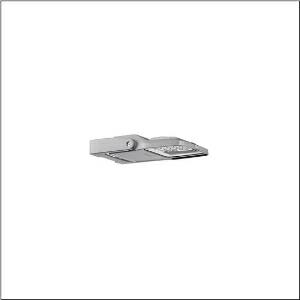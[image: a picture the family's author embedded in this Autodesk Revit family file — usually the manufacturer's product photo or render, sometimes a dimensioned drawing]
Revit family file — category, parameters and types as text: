
# Revit family: floodlight_fl_21_iq_micro___pl33t_5xa7762a2f2a_46b5
name_source: partatom
category: Lighting Fixtures
units: mm (PartAtom-declared; Revit-internal decimal feet)

## family parameters
Cut with Voids When Loaded = No
Host = Face
Light Source = No
Part Type = Normal
Room Calculation Point = No
Round Connector Dimension = Use Diameter
Shared = No

## types (1)
- --- (1 x LED, 2930 lm, 23.1 W, 3000K)
    Apparent Load = 23 VA
    CIE Flux Codes = 26 75 99 100 100
    Color Rendering = 70
    Color Temperature = 3000K
    Default Elevation = 1800 mm
    Description = Floodlight FL 21 iQ micro, floodlight, primary light control with lens, of PMMA, primary optical cover: protective disc, of toughened safety glass, transparent, light distribution: PL33T, light emission: direct distribution, installation type: surface-mounted, LED, High Power LED, rated luminous flux: 2.930lm, luminous efficacy: 127lm/W, light colour: 730, colour temperature: 3000K, control gear: iQ Street-Remote/DALI, control: Auto-Match, Temp-Guard, Night-Set, Smart-Wire, Desk-Remote (wireless, voltage-free reading and setting of iQ features in the workshop via application-optimized NFC function/RFID function), optimised constant luminous flux control (CLO 2.0), Street-Remote, with terminal, 6-pole, mains connection: 220..240V, AC, 50/60Hz, start of lifetime: 23W, end of service life: 24W, reduction: 11W, luminaire housing, of diecast aluminium, powder-coated, Siteco® metallic grey (DB 702S), corrosivity category C5 mid according to DIN EN ISO 12944, suitable for swimming pools, chlorine-resistant, sealing non-destructively replaceable, design bracket, of diecast aluminium, powder-coated, Siteco® metallic grey (DB 702S), protection rating (complete): IP66, insulation class (complete): insulation class II (safety insulation), certification: CE, ENEC, VDE, protection symbol: D, impact resistance: IK07, permissible operating ambient temperature: -40..+40°C, permissible operating ambient temperature for outdoor applications: -40..+50°C, standard: DIN EN 12944, LABS conformity tested according to VDMA 24364:2018-05, packaging unit: 1 piece

Light Distribution: PL33T
    Height = 65 mm
    Lamp = 1 x LED
    Lamp Light Flux = 2930 lm
    Lamp Power = 23.1 W
    Lamp count = 1
    Length = 312 mm
    Luminous efficacy = 127 lm/W
    Manufacturer = Siteco
    ModVariant = No
    Model = 5XA7762A2F2A
    Mounting Place = Wall
    Mounting Type = Surface mounted
    Number of Poles = 1
    OnlyDefault = Yes
    Power Factor = 1
    Product Name = Floodlight FL 21 iQ micro | PL33T
    Product group = floodlight | wall mounted
    ProductGroupID = 2001
    Protection Class = Protection class II
    Protection Degree = IP 66
    RLX_Detail_Level = 1
    RLX_Emergency_Light_Flux = 0 lm
    RLX_Emergency_Type = 0
    RLX_Emergency_Type_DB = No
    RlxData = <blob elided: 97377 chars, md5=efec1c89>
    Socket = socket
    Standby Power = 0 W
    System Light Flux = 2930 lm
    System Power = 23 W
    Type Comments = factory setting: luminous flux: 100 % | dim-lin: 254 | 455 mA
    Type Image = l_1006878.jpg
    URL = http://relux.com
    VarID = @adj_148010
    Voltage = 0 V
    Weight = 0.00 kg
    Width = 230 mm

## geometry (parser evidence)
native form markers: Blend x4, Sweep x14
no freeform markers — native parametric forms only
